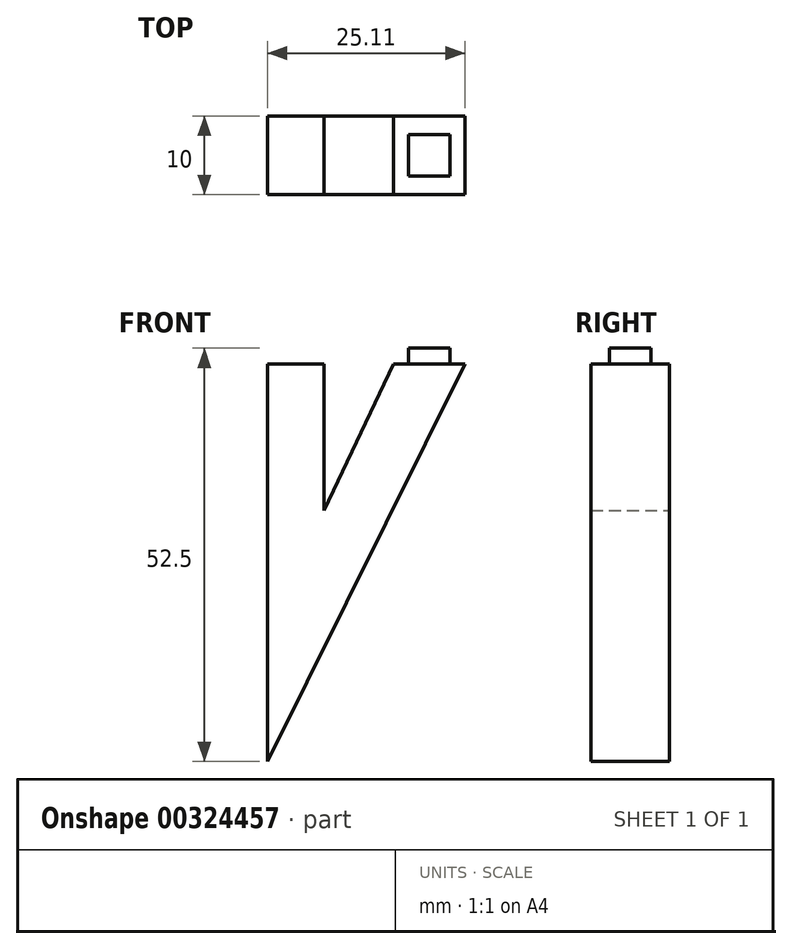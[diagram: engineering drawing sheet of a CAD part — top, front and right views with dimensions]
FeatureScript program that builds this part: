
annotation { "Feature Type Name" : "Feature", "Feature Type Description" : "" }
export const myFeature = defineFeature(function(context is Context, id is Id, definition is map)
    precondition{}
    {
        {
            var Q0;
            Q0=qCreatedBy(makeId("Front.planeOp"),FACE);
            var sketch = newSketch(context, id + "F0", { "sketchPlane" : qUnion([Q0])});
            skLineSegment(sketch, "E0", {"start": v(0, 0) * mm, "end": v(0, -50.5) * mm});
            skLineSegment(sketch, "E1", {"start": v(0, -50.5) * mm, "end": v(25.11, 0) * mm});
            skLineSegment(sketch, "E2", {"start": v(25.11, 0) * mm, "end": v(16.01, 0) * mm});
            skLineSegment(sketch, "E3", {"start": v(0, 0) * mm, "end": v(7.2, 0) * mm});
            skLineSegment(sketch, "E4", {"start": v(7.2, 0) * mm, "end": v(7.2, -18.62) * mm});
            skLineSegment(sketch, "E5", {"start": v(16.01, 0) * mm, "end": v(7.2, -18.62) * mm});
            skSolve(sketch);
        }
        {
            var Q0;
            Q0=makeQuery(id+"F0.imprint","IMPRINT",FACE,{"disambiguationData":[TD([[makeQuery(id+"F0.imprint","IMPRINT",EDGE,{"derivedFrom":sQuery(id+"F0.wireOp",EDGE,"E0")}),1.0]])]});
            extrude(context, id + "F1", {"entities" : qUnion([Q0]), "depth" : 10 * mm});
        }
        {
            var Q0;
            Q0=makeQuery(id+"F1.opExtrude","SWEPT_FACE",FACE,{"disambiguationData":[OSD([sQuery(id+"F0.wireOp",EDGE,"E2")])]});
            var sketch = newSketch(context, id + "F2", { "sketchPlane" : qUnion([Q0])});
            skLineSegment(sketch, "E6", {"start": v(20.56, 0) * mm, "end": v(20.56, -10) * mm});
            skLineSegment(sketch, "E7", {"start": v(16.01, -5) * mm, "end": v(25.11, -5) * mm});
            skLineSegment(sketch, "E8.bottom", {"start": v(23.21, -2.35) * mm, "end": v(17.91, -2.35) * mm});
            skLineSegment(sketch, "E8.top", {"start": v(23.21, -7.65) * mm, "end": v(17.91, -7.65) * mm});
            skLineSegment(sketch, "E8.left", {"start": v(23.21, -2.35) * mm, "end": v(23.21, -7.65) * mm});
            skLineSegment(sketch, "E8.right", {"start": v(17.91, -2.35) * mm, "end": v(17.91, -7.65) * mm});
            skPoint(sketch, "E8.middle", {"position": v(20.56, -5) * mm});
            skSolve(sketch);
        }
        {
            var Q0;
            Q0 = qSketchRegion(id + "F2", true);
            extrude(context, id + "F3", {"entities" : qUnion([Q0]), "operationType" : NewBodyOperationType.ADD, "depth" : 2 * mm});
        }
    });
